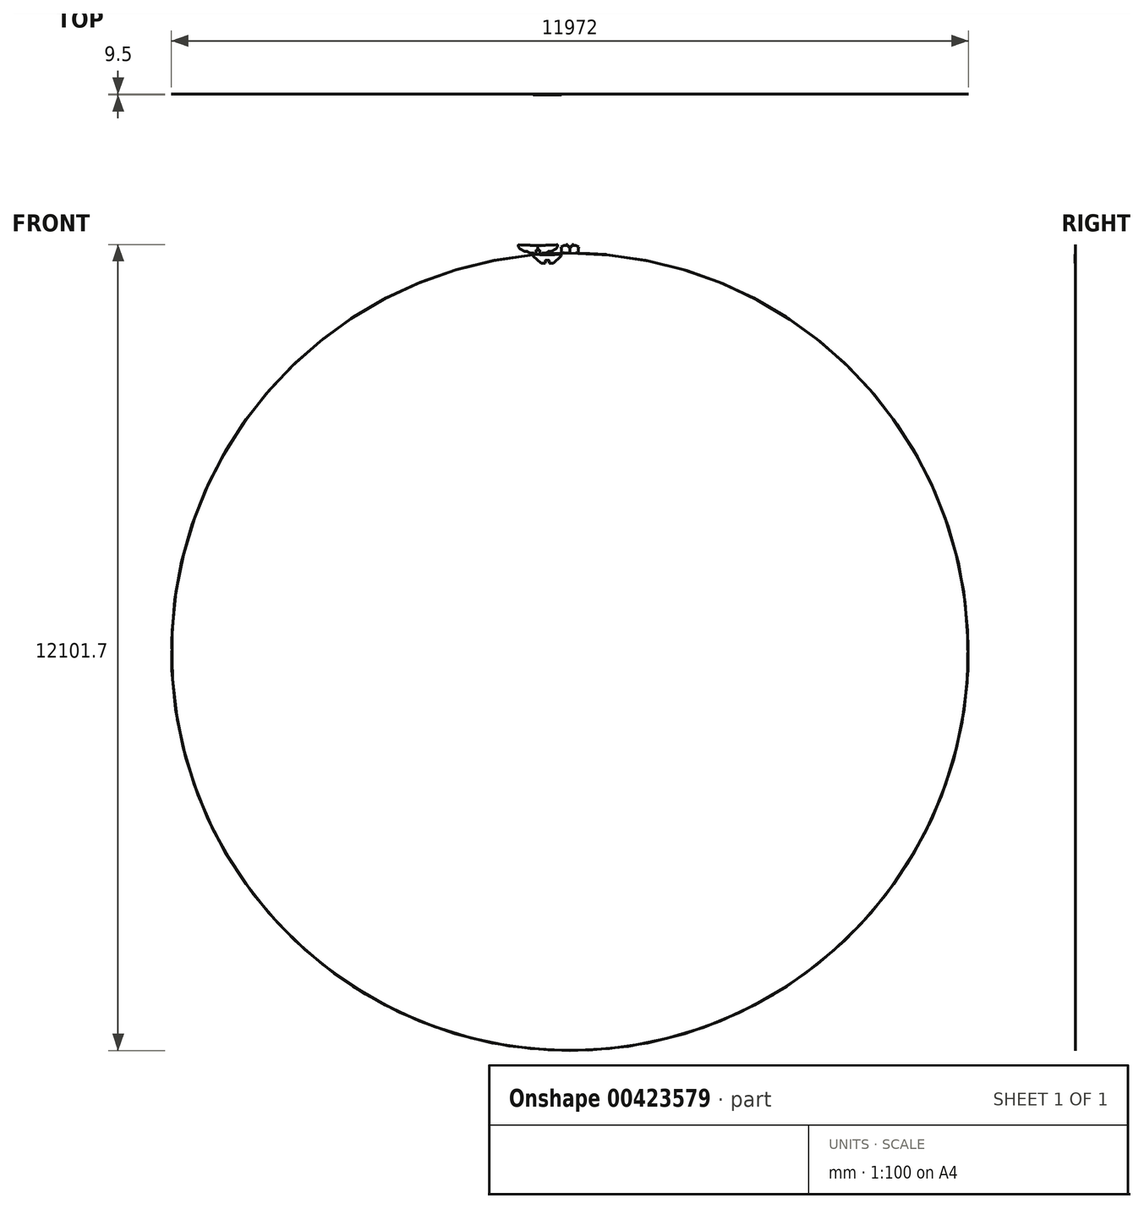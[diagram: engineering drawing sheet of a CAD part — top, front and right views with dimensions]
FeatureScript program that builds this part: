
annotation { "Feature Type Name" : "Feature", "Feature Type Description" : "" }
export const myFeature = defineFeature(function(context is Context, id is Id, definition is map)
    precondition{}
    {
        {
            assignVariable(context, id + "F0", {"name" : "eTole", "anyValue" : 1});
        }
        {
            assignVariable(context, id + "F1", {"name" : "eProfil", "anyValue" : 7});
        }
        {
            var Q0;
            Q0=qCreatedBy(makeId("Front.planeOp"),FACE);
            var sketch = newSketch(context, id + "F2", { "sketchPlane" : qUnion([Q0])});
            skLineSegment(sketch, "E0.bottom", {"start": v(-500, 75) * mm, "end": v(500, 75) * mm});
            skLineSegment(sketch, "E0.top", {"start": v(-500, -75) * mm, "end": v(500, -75) * mm});
            skLineSegment(sketch, "E0.left", {"start": v(-500, 75) * mm, "end": v(-500, -75) * mm});
            skLineSegment(sketch, "E0.right", {"start": v(500, 75) * mm, "end": v(500, -75) * mm});
            skCircle(sketch, "E1", {"center": v(-140, -3) * mm, "radius": 4 * mm});
            skCircle(sketch, "E2", {"center": v(340, 26) * mm, "radius": 4 * mm});
            skLineSegment(sketch, "E3.bottom", {"start": v(-255, -75) * mm, "end": v(261.67, -75) * mm});
            skLineSegment(sketch, "E3.top", {"start": v(-255, -225) * mm, "end": v(228.33, -225) * mm});
            skLineSegment(sketch, "E3.left", {"start": v(-255, -75) * mm, "end": v(-255, -225) * mm});
            skLineSegment(sketch, "E3.right", {"start": v(261.67, -75) * mm, "end": v(228.33, -225) * mm});
            skCircle(sketch, "E4", {"center": v(0, -155) * mm, "radius": 4 * mm});
            skLineSegment(sketch, "E5", {"start": v(-255, -150) * mm, "end": v(245, -150) * mm, "construction": true});
            skPoint(sketch, "E6", {"position": v(0, -105) * mm});
            skLineSegment(sketch, "E7", {"start": v(-255, -105) * mm, "end": v(255, -105) * mm, "construction": true});
            skSolve(sketch);
        }
        {
            var Q0;
            Q0=sQuery(id+"F2.wireOp",VERTEX,"E1.center");
            var Q1;
            Q1=qCreatedBy(makeId("Right.planeOp"),FACE);
            cPlane(context, id + "F3", {"entities" : qUnion([Q0, Q1]), "cplaneType" : CPlaneType.PLANE_POINT, "offset" : 25 * mm, "width" : 150 * mm, "height" : 150 * mm});
        }
        {
            var Q0;
            Q0=sQuery(id+"F2.wireOp",VERTEX,"E2.center");
            var Q1;
            Q1=qCreatedBy(makeId("Right.planeOp"),FACE);
            cPlane(context, id + "F4", {"entities" : qUnion([Q0, Q1]), "cplaneType" : CPlaneType.PLANE_POINT, "offset" : 25 * mm, "width" : 150 * mm, "height" : 150 * mm});
        }
        {
            var Q0;
            Q0=qCreatedBy(makeId("Front.planeOp"),FACE);
            var sketch = newSketch(context, id + "F5", { "sketchPlane" : qUnion([Q0])});
            skCircle(sketch, "E8.0", {"center": v(-140, -3) * mm, "radius": 4 * mm});
            skLineSegment(sketch, "E9.bottom", {"start": v(-164, -13) * mm, "end": v(-116, -13) * mm});
            skLineSegment(sketch, "E9.top", {"start": v(-164, -73) * mm, "end": v(-116, -73) * mm});
            skLineSegment(sketch, "E9.left", {"start": v(-170, -19) * mm, "end": v(-170, -67) * mm});
            skLineSegment(sketch, "E9.right", {"start": v(-110, -19) * mm, "end": v(-110, -67) * mm});
            skLineSegment(sketch, "E10", {"start": v(-140, -3) * mm, "end": v(-140, -73) * mm, "construction": true});
            skPoint(sketch, "E11.visualSharp", {"position": v(-170, -13) * mm});
            skArc(sketch, "E11.filletArc", {"start": v(-164, -13) * mm, "mid": v(-168.24, -14.76) * mm, "end": v(-170, -19) * mm});
            skPoint(sketch, "E12.visualSharp", {"position": v(-170, -73) * mm});
            skArc(sketch, "E12.filletArc", {"start": v(-170, -67) * mm, "mid": v(-168.24, -71.24) * mm, "end": v(-164, -73) * mm});
            skPoint(sketch, "E13.visualSharp", {"position": v(-110, -73) * mm});
            skArc(sketch, "E13.filletArc", {"start": v(-116, -73) * mm, "mid": v(-111.76, -71.24) * mm, "end": v(-110, -67) * mm});
            skPoint(sketch, "E14.visualSharp", {"position": v(-110, -13) * mm});
            skArc(sketch, "E14.filletArc", {"start": v(-110, -19) * mm, "mid": v(-111.76, -14.76) * mm, "end": v(-116, -13) * mm});
            skLineSegment(sketch, "E15.bottom", {"start": v(316, 96) * mm, "end": v(364, 96) * mm});
            skLineSegment(sketch, "E15.top", {"start": v(316, 36) * mm, "end": v(364, 36) * mm});
            skLineSegment(sketch, "E15.left", {"start": v(310, 90) * mm, "end": v(310, 42) * mm});
            skLineSegment(sketch, "E15.right", {"start": v(370, 90) * mm, "end": v(370, 42) * mm});
            skPoint(sketch, "E16.visualSharp", {"position": v(310, 96) * mm});
            skArc(sketch, "E16.filletArc", {"start": v(316, 96) * mm, "mid": v(311.76, 94.24) * mm, "end": v(310, 90) * mm});
            skPoint(sketch, "E17.visualSharp", {"position": v(310, 36) * mm});
            skArc(sketch, "E17.filletArc", {"start": v(310, 42) * mm, "mid": v(311.76, 37.76) * mm, "end": v(316, 36) * mm});
            skPoint(sketch, "E18.visualSharp", {"position": v(370, 36) * mm});
            skArc(sketch, "E18.filletArc", {"start": v(364, 36) * mm, "mid": v(368.24, 37.76) * mm, "end": v(370, 42) * mm});
            skPoint(sketch, "E19.visualSharp", {"position": v(370, 96) * mm});
            skArc(sketch, "E19.filletArc", {"start": v(370, 90) * mm, "mid": v(368.24, 94.24) * mm, "end": v(364, 96) * mm});
            skCircle(sketch, "E20.0", {"center": v(340, 26) * mm, "radius": 4 * mm});
            skLineSegment(sketch, "E21", {"start": v(340, 26) * mm, "end": v(340, 96) * mm, "construction": true});
            skLineSegment(sketch, "E22", {"start": v(-215, -73) * mm, "end": v(-215, 57) * mm, "construction": true});
            skLineSegment(sketch, "E23.MirrorCS", {"start": v(-65, -73) * mm, "end": v(-65, 57) * mm, "construction": true});
            skLineSegment(sketch, "E24.bottom", {"start": v(-80, -58) * mm, "end": v(-50, -58) * mm, "construction": true});
            skLineSegment(sketch, "E24.top", {"start": v(-80, -73) * mm, "end": v(-50, -73) * mm, "construction": true});
            skLineSegment(sketch, "E24.left", {"start": v(-80, -58) * mm, "end": v(-80, -73) * mm, "construction": true});
            skLineSegment(sketch, "E24.right", {"start": v(-50, -58) * mm, "end": v(-50, -73) * mm, "construction": true});
            skLineSegment(sketch, "E25.bottom", {"start": v(250, 96) * mm, "end": v(280, 96) * mm, "construction": true});
            skLineSegment(sketch, "E25.top", {"start": v(250, 81) * mm, "end": v(280, 81) * mm, "construction": true});
            skLineSegment(sketch, "E25.left", {"start": v(250, 96) * mm, "end": v(250, 81) * mm, "construction": true});
            skLineSegment(sketch, "E25.right", {"start": v(280, 96) * mm, "end": v(280, 81) * mm, "construction": true});
            skLineSegment(sketch, "E26", {"start": v(280, 81) * mm, "end": v(310, 81) * mm, "construction": true});
            skLineSegment(sketch, "E27", {"start": v(-110, -58) * mm, "end": v(-80, -58) * mm, "construction": true});
            skLineSegment(sketch, "E28", {"start": v(265, 96) * mm, "end": v(265, -34) * mm, "construction": true});
            skCircle(sketch, "E29.0", {"center": v(0, -155) * mm, "radius": 4 * mm});
            skLineSegment(sketch, "E30.bottom", {"start": v(-24, -165) * mm, "end": v(24, -165) * mm});
            skLineSegment(sketch, "E30.top", {"start": v(-24, -225) * mm, "end": v(24, -225) * mm});
            skLineSegment(sketch, "E30.left", {"start": v(-30, -171) * mm, "end": v(-30, -219) * mm});
            skLineSegment(sketch, "E30.right", {"start": v(30, -171) * mm, "end": v(30, -219) * mm});
            skLineSegment(sketch, "E31", {"start": v(0, -155) * mm, "end": v(0, -225) * mm, "construction": true});
            skPoint(sketch, "E32.visualSharp", {"position": v(-30, -225) * mm});
            skArc(sketch, "E32.filletArc", {"start": v(-30, -219) * mm, "mid": v(-28.24, -223.24) * mm, "end": v(-24, -225) * mm});
            skPoint(sketch, "E33.visualSharp", {"position": v(-30, -165) * mm});
            skArc(sketch, "E33.filletArc", {"start": v(-24, -165) * mm, "mid": v(-28.24, -166.76) * mm, "end": v(-30, -171) * mm});
            skPoint(sketch, "E34.visualSharp", {"position": v(30, -165) * mm});
            skArc(sketch, "E34.filletArc", {"start": v(30, -171) * mm, "mid": v(28.24, -166.76) * mm, "end": v(24, -165) * mm});
            skPoint(sketch, "E35.visualSharp", {"position": v(30, -225) * mm});
            skArc(sketch, "E35.filletArc", {"start": v(24, -225) * mm, "mid": v(28.24, -223.24) * mm, "end": v(30, -219) * mm});
            skLineSegment(sketch, "E36.MirrorCS", {"start": v(75, -225) * mm, "end": v(75, -95) * mm, "construction": true});
            skLineSegment(sketch, "E37.bottom", {"start": v(60, -210) * mm, "end": v(90, -210) * mm, "construction": true});
            skLineSegment(sketch, "E37.top", {"start": v(60, -225) * mm, "end": v(90, -225) * mm, "construction": true});
            skLineSegment(sketch, "E37.left", {"start": v(60, -210) * mm, "end": v(60, -225) * mm, "construction": true});
            skLineSegment(sketch, "E37.right", {"start": v(90, -210) * mm, "end": v(90, -225) * mm, "construction": true});
            skLineSegment(sketch, "E38", {"start": v(30, -210) * mm, "end": v(60, -210) * mm, "construction": true});
            skSolve(sketch);
        }
        {
            var Q0;
            Q0=qCreatedBy(makeId("Front.planeOp"),FACE);
            var sketch = newSketch(context, id + "F6", { "sketchPlane" : qUnion([Q0])});
            skLineSegment(sketch, "E39.0", {"start": v(-140, 1) * mm, "end": v(-140, 1) * mm});
            skLineSegment(sketch, "E39.1", {"start": v(-140, -13) * mm, "end": v(-116, -13) * mm});
            skLineSegment(sketch, "E39.2", {"start": v(-110, -19) * mm, "end": v(-110, -72.6) * mm});
            skArc(sketch, "E39.3", {"start": v(-110, -19) * mm, "mid": v(-111.76, -14.76) * mm, "end": v(-116, -13) * mm});
            skLineSegment(sketch, "E40", {"start": v(-140, -13) * mm, "end": v(-140, -7) * mm});
            skLineSegment(sketch, "E41.trimOffspring", {"start": v(-140, 1) * mm, "end": v(-140, 57) * mm});
            skLineSegment(sketch, "E42.0", {"start": v(-80, -58) * mm, "end": v(-80, -73) * mm, "construction": true});
            skLineSegment(sketch, "E42.1", {"start": v(-80, -73) * mm, "end": v(-50, -73) * mm, "construction": true});
            skLineSegment(sketch, "E43", {"start": v(-67.3, 57.64) * mm, "end": v(-65, -72.34) * mm, "construction": true});
            skLineSegment(sketch, "E44", {"start": v(-82.3, 57.38) * mm, "end": v(-52.3, 57.9) * mm, "construction": true});
            skLineSegment(sketch, "E45", {"start": v(-80, -72.6) * mm, "end": v(-50, -72.07) * mm, "construction": true});
            skLineSegment(sketch, "E46.0", {"start": v(-65, -73) * mm, "end": v(-65, 57) * mm, "construction": true});
            skArc(sketch, "E47", {"start": v(-140, 57) * mm, "mid": v(-112.14, 57.1) * mm, "end": v(-84.29, 57.38) * mm});
            skLineSegment(sketch, "E48", {"start": v(152.25, 67.4) * mm, "end": v(152.28, 67.07) * mm, "construction": true});
            skLineSegment(sketch, "E49", {"start": v(152.28, 67.07) * mm, "end": v(124.54, 65.2) * mm});
            skLineSegment(sketch, "E50", {"start": v(123.17, 64.51) * mm, "end": v(117.13, 57.6) * mm});
            skLineSegment(sketch, "E51", {"start": v(152.28, 67.07) * mm, "end": v(154.16, 39.33) * mm, "construction": true});
            skLineSegment(sketch, "E52", {"start": v(155.6, 40.12) * mm, "end": v(154.16, 39.33) * mm});
            skLineSegment(sketch, "E53", {"start": v(137.97, 66.4) * mm, "end": v(138, 66.1) * mm, "construction": true});
            skArc(sketch, "E54", {"start": v(117.13, 57.6) * mm, "mid": v(114.67, 60.86) * mm, "end": v(113.72, 64.83) * mm});
            skLineSegment(sketch, "E55", {"start": v(-80, -72.6) * mm, "end": v(-110, -72.6) * mm});
            skLineSegment(sketch, "E56", {"start": v(-80, -72.6) * mm, "end": v(-80.26, -57.6) * mm});
            skLineSegment(sketch, "E57", {"start": v(-80.26, -57.6) * mm, "end": v(-21.59, -56.57) * mm});
            skLineSegment(sketch, "E58", {"start": v(16.3, -35.9) * mm, "end": v(59.45, -35.13) * mm});
            skLineSegment(sketch, "E59", {"start": v(59.45, -35.13) * mm, "end": v(128.97, 2.8) * mm});
            skLineSegment(sketch, "E60", {"start": v(128.97, 2.8) * mm, "end": v(152.96, 38.68) * mm});
            skLineSegment(sketch, "E61", {"start": v(12.7, -35.58) * mm, "end": v(15.34, -34.14) * mm});
            skLineSegment(sketch, "E62", {"start": v(15.34, -34.14) * mm, "end": v(16.3, -35.9) * mm});
            skLineSegment(sketch, "E63", {"start": v(152.96, 38.68) * mm, "end": v(152, 40.44) * mm});
            skLineSegment(sketch, "E64", {"start": v(152, 40.44) * mm, "end": v(154.63, 41.87) * mm});
            skLineSegment(sketch, "E65", {"start": v(154.63, 41.87) * mm, "end": v(155.6, 40.12) * mm});
            skLineSegment(sketch, "E66.trimOffspring", {"start": v(152.96, 38.68) * mm, "end": v(16.3, -35.9) * mm, "construction": true});
            skLineSegment(sketch, "E67", {"start": v(-82.26, 55.41) * mm, "end": v(-81.96, 38.38) * mm});
            skLineSegment(sketch, "E68", {"start": v(-81.96, 38.38) * mm, "end": v(-80.96, 38.4) * mm});
            skLineSegment(sketch, "E69", {"start": v(-80.96, 38.4) * mm, "end": v(-81.23, 53.4) * mm});
            skLineSegment(sketch, "E70", {"start": v(-79.26, 55.43) * mm, "end": v(-55.26, 55.86) * mm});
            skLineSegment(sketch, "E71", {"start": v(-53.23, 53.9) * mm, "end": v(-52.96, 38.9) * mm});
            skLineSegment(sketch, "E72", {"start": v(-52.96, 38.9) * mm, "end": v(-51.96, 38.91) * mm});
            skLineSegment(sketch, "E73", {"start": v(-51.96, 38.91) * mm, "end": v(-52.27, 55.94) * mm});
            skLineSegment(sketch, "E74", {"start": v(154.41, 65.14) * mm, "end": v(155.2, 41.16) * mm});
            skArc(sketch, "E75", {"start": v(154.16, 39.33) * mm, "mid": v(154.93, 40.1) * mm, "end": v(155.2, 41.16) * mm});
            skArc(sketch, "E76", {"start": v(152.28, 67.07) * mm, "mid": v(153.75, 66.56) * mm, "end": v(154.41, 65.14) * mm});
            skArc(sketch, "E77.filletArc", {"start": v(124.54, 65.2) * mm, "mid": v(123.79, 64.99) * mm, "end": v(123.17, 64.51) * mm});
            skArc(sketch, "E78.trimOffspring", {"start": v(-50.3, 57.98) * mm, "mid": v(31.74, 60.59) * mm, "end": v(113.72, 64.83) * mm});
            skPoint(sketch, "E79.visualSharp", {"position": v(-81.26, 55.4) * mm});
            skArc(sketch, "E79.filletArc", {"start": v(-79.26, 55.43) * mm, "mid": v(-80.66, 54.82) * mm, "end": v(-81.23, 53.4) * mm});
            skPoint(sketch, "E80.visualSharp", {"position": v(-53.26, 55.9) * mm});
            skArc(sketch, "E80.filletArc", {"start": v(-53.23, 53.9) * mm, "mid": v(-53.84, 55.3) * mm, "end": v(-55.26, 55.86) * mm});
            skPoint(sketch, "E81.visualSharp", {"position": v(-82.3, 57.4) * mm});
            skArc(sketch, "E81.filletArc", {"start": v(-82.26, 55.41) * mm, "mid": v(-82.87, 56.81) * mm, "end": v(-84.29, 57.38) * mm});
            skPoint(sketch, "E82.visualSharp", {"position": v(-52.3, 57.94) * mm});
            skArc(sketch, "E82.filletArc", {"start": v(-50.3, 57.98) * mm, "mid": v(-51.7, 57.36) * mm, "end": v(-52.27, 55.94) * mm});
            skArc(sketch, "E83.0", {"start": v(-140, -7) * mm, "mid": v(-136, -3) * mm, "end": v(-140, 1) * mm});
            skLineSegment(sketch, "E84", {"start": v(12.7, -35.58) * mm, "end": v(13.66, -37.33) * mm});
            skLineSegment(sketch, "E85", {"start": v(13.66, -37.33) * mm, "end": v(-21.59, -56.57) * mm});
            skSolve(sketch);
        }
        {
            var Q0;
            Q0=qCreatedBy(makeId("Front.planeOp"),FACE);
            var sketch = newSketch(context, id + "F7", { "sketchPlane" : qUnion([Q0])});
            skLineSegment(sketch, "E86.0", {"start": v(0, -151) * mm, "end": v(0, -151) * mm});
            skLineSegment(sketch, "E87.0", {"start": v(0, -165) * mm, "end": v(24, -165) * mm});
            skArc(sketch, "E87.1", {"start": v(30, -171) * mm, "mid": v(28.24, -166.76) * mm, "end": v(24, -165) * mm});
            skLineSegment(sketch, "E87.2", {"start": v(30, -171) * mm, "end": v(30, -212.17) * mm});
            skLineSegment(sketch, "E88", {"start": v(0, -165) * mm, "end": v(0, -151) * mm});
            skLineSegment(sketch, "E89.trimOffspring", {"start": v(0, -151) * mm, "end": v(0, -82.5) * mm});
            skLineSegment(sketch, "E90.0", {"start": v(75, -225) * mm, "end": v(75, -95) * mm, "construction": true});
            skLineSegment(sketch, "E90.1", {"start": v(60, -225) * mm, "end": v(90, -225) * mm, "construction": true});
            skLineSegment(sketch, "E90.2", {"start": v(90, -210) * mm, "end": v(90, -225) * mm, "construction": true});
            skArc(sketch, "E91", {"start": v(0, -82.5) * mm, "mid": v(28.05, -82.42) * mm, "end": v(56.1, -82.18) * mm});
            skLineSegment(sketch, "E92", {"start": v(207.44, -78.17) * mm, "end": v(207.45, -78.5) * mm, "construction": true});
            skLineSegment(sketch, "E93", {"start": v(73.09, -81.96) * mm, "end": v(75, -211.95) * mm, "construction": true});
            skLineSegment(sketch, "E94", {"start": v(60, -212.17) * mm, "end": v(90, -211.73) * mm, "construction": true});
            skLineSegment(sketch, "E95", {"start": v(60, -212.17) * mm, "end": v(30, -212.17) * mm});
            skLineSegment(sketch, "E96", {"start": v(60, -212.17) * mm, "end": v(59.78, -197.17) * mm});
            skLineSegment(sketch, "E97", {"start": v(59.78, -197.17) * mm, "end": v(104.21, -196.52) * mm});
            skLineSegment(sketch, "E98", {"start": v(171.22, -86.97) * mm, "end": v(177.45, -80.24) * mm});
            skLineSegment(sketch, "E99", {"start": v(178.84, -79.6) * mm, "end": v(207.45, -78.5) * mm});
            skLineSegment(sketch, "E100", {"start": v(192.73, -79.06) * mm, "end": v(192.72, -78.76) * mm, "construction": true});
            skLineSegment(sketch, "E101", {"start": v(90, -211.73) * mm, "end": v(208.56, -107.1) * mm, "construction": true});
            skArc(sketch, "E102", {"start": v(171.22, -86.97) * mm, "mid": v(168.85, -83.65) * mm, "end": v(168, -79.66) * mm});
            skLineSegment(sketch, "E103", {"start": v(104.21, -196.52) * mm, "end": v(110.84, -190.67) * mm});
            skLineSegment(sketch, "E104", {"start": v(110.84, -190.67) * mm, "end": v(112.16, -192.17) * mm});
            skLineSegment(sketch, "E105", {"start": v(112.16, -192.17) * mm, "end": v(142.4, -192.17) * mm});
            skLineSegment(sketch, "E106", {"start": v(142.4, -192.17) * mm, "end": v(201.6, -139.93) * mm});
            skLineSegment(sketch, "E107", {"start": v(201.6, -139.93) * mm, "end": v(205.36, -109.94) * mm});
            skLineSegment(sketch, "E108", {"start": v(205.36, -109.94) * mm, "end": v(204.03, -108.44) * mm});
            skLineSegment(sketch, "E109", {"start": v(204.03, -108.44) * mm, "end": v(206.28, -106.45) * mm});
            skLineSegment(sketch, "E110", {"start": v(206.28, -106.45) * mm, "end": v(207.6, -107.95) * mm});
            skLineSegment(sketch, "E111", {"start": v(209.53, -80.4) * mm, "end": v(210.53, -104.39) * mm});
            skArc(sketch, "E112", {"start": v(209.53, -80.4) * mm, "mid": v(208.89, -79.02) * mm, "end": v(207.45, -78.5) * mm});
            skLineSegment(sketch, "E113", {"start": v(207.6, -107.95) * mm, "end": v(209.86, -105.97) * mm});
            skArc(sketch, "E114", {"start": v(210.53, -104.39) * mm, "mid": v(210.37, -105.25) * mm, "end": v(209.86, -105.97) * mm});
            skLineSegment(sketch, "E115.trimOffspring", {"start": v(207.45, -78.5) * mm, "end": v(208.56, -107.1) * mm, "construction": true});
            skLineSegment(sketch, "E116", {"start": v(58.1, -82.18) * mm, "end": v(88.09, -81.74) * mm, "construction": true});
            skLineSegment(sketch, "E117", {"start": v(58.12, -84.15) * mm, "end": v(58.34, -99.18) * mm});
            skLineSegment(sketch, "E118", {"start": v(58.34, -99.18) * mm, "end": v(59.34, -99.17) * mm});
            skLineSegment(sketch, "E119", {"start": v(59.15, -86.17) * mm, "end": v(59.34, -99.17) * mm});
            skLineSegment(sketch, "E120", {"start": v(61.12, -84.14) * mm, "end": v(85.12, -83.79) * mm});
            skLineSegment(sketch, "E121", {"start": v(87.34, -98.75) * mm, "end": v(87.15, -85.76) * mm});
            skLineSegment(sketch, "E122", {"start": v(87.34, -98.75) * mm, "end": v(88.34, -98.74) * mm});
            skLineSegment(sketch, "E123", {"start": v(88.34, -98.74) * mm, "end": v(88.12, -83.71) * mm});
            skArc(sketch, "E124.trimOffspring", {"start": v(90.08, -81.68) * mm, "mid": v(129.05, -80.82) * mm, "end": v(168, -79.66) * mm});
            skPoint(sketch, "E125.visualSharp", {"position": v(59.12, -84.17) * mm});
            skArc(sketch, "E125.filletArc", {"start": v(61.12, -84.14) * mm, "mid": v(59.71, -84.75) * mm, "end": v(59.15, -86.17) * mm});
            skPoint(sketch, "E126.visualSharp", {"position": v(87.12, -83.76) * mm});
            skArc(sketch, "E126.filletArc", {"start": v(87.15, -85.76) * mm, "mid": v(86.54, -84.35) * mm, "end": v(85.12, -83.79) * mm});
            skPoint(sketch, "E127.visualSharp", {"position": v(58.09, -82.16) * mm});
            skArc(sketch, "E127.filletArc", {"start": v(58.12, -84.15) * mm, "mid": v(57.52, -82.75) * mm, "end": v(56.1, -82.18) * mm});
            skPoint(sketch, "E128.visualSharp", {"position": v(88.09, -81.72) * mm});
            skArc(sketch, "E128.filletArc", {"start": v(90.08, -81.68) * mm, "mid": v(88.68, -82.3) * mm, "end": v(88.12, -83.71) * mm});
            skArc(sketch, "E129.filletArc", {"start": v(178.84, -79.6) * mm, "mid": v(178.08, -79.78) * mm, "end": v(177.45, -80.24) * mm});
            skSolve(sketch);
        }
        {
            var Q0;
            Q0=qCreatedBy(makeId("Front.planeOp"),FACE);
            var sketch = newSketch(context, id + "F8", { "sketchPlane" : qUnion([Q0])});
            skLineSegment(sketch, "E130.0", {"start": v(310, 69.52) * mm, "end": v(310, 42) * mm});
            skLineSegment(sketch, "E130.1", {"start": v(316, 36) * mm, "end": v(340, 36) * mm});
            skLineSegment(sketch, "E130.2", {"start": v(340, 30) * mm, "end": v(340, 30) * mm});
            skArc(sketch, "E130.3", {"start": v(310, 42) * mm, "mid": v(311.76, 37.76) * mm, "end": v(316, 36) * mm});
            skLineSegment(sketch, "E130.4", {"start": v(250, 96) * mm, "end": v(280, 96) * mm, "construction": true});
            skLineSegment(sketch, "E130.5", {"start": v(265, 96) * mm, "end": v(265, -34) * mm, "construction": true});
            skLineSegment(sketch, "E130.6", {"start": v(280, 96) * mm, "end": v(280, 81) * mm, "construction": true});
            skLineSegment(sketch, "E131", {"start": v(340, 36) * mm, "end": v(340, 30) * mm});
            skLineSegment(sketch, "E132.trimOffspring", {"start": v(340, 22) * mm, "end": v(340, -60.2) * mm});
            skArc(sketch, "E133", {"start": v(340, -60.2) * mm, "mid": v(311.8, -60.27) * mm, "end": v(283.59, -60.47) * mm});
            skLineSegment(sketch, "E134", {"start": v(266.6, -60.65) * mm, "end": v(265, 69.34) * mm, "construction": true});
            skLineSegment(sketch, "E135", {"start": v(250, 69.16) * mm, "end": v(280, 69.52) * mm, "construction": true});
            skLineSegment(sketch, "E136", {"start": v(280, 69.52) * mm, "end": v(310, 69.52) * mm});
            skLineSegment(sketch, "E137", {"start": v(215, -61.5) * mm, "end": v(215, -61.2) * mm, "construction": true});
            skLineSegment(sketch, "E138", {"start": v(246.76, -53.52) * mm, "end": v(240.4, -60.13) * mm});
            skLineSegment(sketch, "E139", {"start": v(239, -60.74) * mm, "end": v(215, -61.2) * mm});
            skLineSegment(sketch, "E140", {"start": v(215, -61.2) * mm, "end": v(214.42, -30.35) * mm, "construction": true});
            skLineSegment(sketch, "E141", {"start": v(240.89, 54.04) * mm, "end": v(280.18, 54.53) * mm});
            skLineSegment(sketch, "E142", {"start": v(280.18, 54.53) * mm, "end": v(280, 69.52) * mm});
            skLineSegment(sketch, "E143", {"start": v(227.41, -60.96) * mm, "end": v(227.42, -61.26) * mm, "construction": true});
            skArc(sketch, "E144", {"start": v(246.76, -53.52) * mm, "mid": v(249.06, -56.88) * mm, "end": v(249.83, -60.88) * mm});
            skLineSegment(sketch, "E145", {"start": v(251.6, -60.83) * mm, "end": v(281.6, -60.47) * mm, "construction": true});
            skLineSegment(sketch, "E146", {"start": v(251.37, -42.71) * mm, "end": v(251.57, -58.86) * mm});
            skLineSegment(sketch, "E147", {"start": v(251.37, -42.71) * mm, "end": v(252.37, -42.7) * mm});
            skLineSegment(sketch, "E148", {"start": v(252.37, -42.7) * mm, "end": v(252.55, -56.82) * mm});
            skLineSegment(sketch, "E149", {"start": v(254.57, -58.8) * mm, "end": v(278.57, -58.5) * mm});
            skLineSegment(sketch, "E150", {"start": v(280.54, -56.48) * mm, "end": v(280.37, -42.36) * mm});
            skLineSegment(sketch, "E151", {"start": v(280.37, -42.36) * mm, "end": v(281.37, -42.35) * mm});
            skLineSegment(sketch, "E152", {"start": v(281.57, -58.5) * mm, "end": v(281.37, -42.35) * mm});
            skArc(sketch, "E153.trimOffspring", {"start": v(249.6, -60.88) * mm, "mid": v(430.29, -12031.52) * mm, "end": v(249.83, -60.88) * mm});
            skLineSegment(sketch, "E154", {"start": v(243.24, 54.07) * mm, "end": v(242.33, 51.21) * mm});
            skLineSegment(sketch, "E155", {"start": v(242.33, 51.21) * mm, "end": v(240.43, 51.82) * mm});
            skLineSegment(sketch, "E156", {"start": v(240.43, 51.82) * mm, "end": v(207.85, 35.55) * mm});
            skLineSegment(sketch, "E157", {"start": v(207.85, 35.55) * mm, "end": v(213.74, 6.06) * mm});
            skLineSegment(sketch, "E158", {"start": v(213.74, 6.06) * mm, "end": v(214.42, -30.35) * mm});
            skLineSegment(sketch, "E159", {"start": v(214.42, -30.35) * mm, "end": v(216.1, -31.43) * mm});
            skLineSegment(sketch, "E160", {"start": v(216.1, -31.43) * mm, "end": v(214.5, -33.95) * mm});
            skLineSegment(sketch, "E161", {"start": v(214.5, -33.95) * mm, "end": v(213.09, -33.45) * mm});
            skLineSegment(sketch, "E162", {"start": v(213.09, -33.45) * mm, "end": v(212.68, -34.4) * mm});
            skLineSegment(sketch, "E163", {"start": v(212.97, -59.23) * mm, "end": v(212.51, -35.23) * mm});
            skArc(sketch, "E164", {"start": v(215, -61.2) * mm, "mid": v(213.58, -60.63) * mm, "end": v(212.97, -59.23) * mm});
            skPoint(sketch, "E165.visualSharp", {"position": v(212.5, -34.8) * mm});
            skArc(sketch, "E165.filletArc", {"start": v(212.68, -34.4) * mm, "mid": v(212.55, -34.81) * mm, "end": v(212.51, -35.23) * mm});
            skArc(sketch, "E166.0", {"start": v(340, 30) * mm, "mid": v(336, 26) * mm, "end": v(340, 22) * mm});
            skPoint(sketch, "E167.visualSharp", {"position": v(251.6, -60.85) * mm});
            skArc(sketch, "E167.filletArc", {"start": v(249.6, -60.88) * mm, "mid": v(251, -60.28) * mm, "end": v(251.57, -58.86) * mm});
            skPoint(sketch, "E168.visualSharp", {"position": v(252.57, -58.82) * mm});
            skArc(sketch, "E168.filletArc", {"start": v(252.55, -56.82) * mm, "mid": v(253.15, -58.23) * mm, "end": v(254.57, -58.8) * mm});
            skPoint(sketch, "E169.visualSharp", {"position": v(280.57, -58.48) * mm});
            skArc(sketch, "E169.filletArc", {"start": v(278.57, -58.5) * mm, "mid": v(279.98, -57.9) * mm, "end": v(280.54, -56.48) * mm});
            skPoint(sketch, "E170.visualSharp", {"position": v(281.6, -60.48) * mm});
            skArc(sketch, "E170.filletArc", {"start": v(281.57, -58.5) * mm, "mid": v(282.17, -59.9) * mm, "end": v(283.59, -60.47) * mm});
            skArc(sketch, "E171.filletArc", {"start": v(239, -60.74) * mm, "mid": v(239.76, -60.57) * mm, "end": v(240.4, -60.13) * mm});
            skLineSegment(sketch, "E172", {"start": v(250, 69.16) * mm, "end": v(214.42, -30.35) * mm, "construction": true});
            skLineSegment(sketch, "E173", {"start": v(214.96, -59.2) * mm, "end": v(238.96, -58.74) * mm, "construction": true});
            skSolve(sketch);
        }
        {
            var Q0;
            Q0=qCreatedBy(makeId("Front.planeOp"),FACE);
            var sketch = newSketch(context, id + "F9", { "sketchPlane" : qUnion([Q0])});
            skLineSegment(sketch, "E174.0", {"start": v(-140, 1) * mm, "end": v(-140, 57) * mm, "construction": true});
            skLineSegment(sketch, "E175.0", {"start": v(-80, -72.6) * mm, "end": v(-80.26, -57.6) * mm});
            skLineSegment(sketch, "E175.1", {"start": v(-80.26, -57.6) * mm, "end": v(-21.59, -56.57) * mm});
            skLineSegment(sketch, "E175.2", {"start": v(59.45, -35.13) * mm, "end": v(128.97, 2.8) * mm});
            skLineSegment(sketch, "E175.3", {"start": v(128.97, 2.8) * mm, "end": v(152.96, 38.68) * mm});
            skLineSegment(sketch, "E175.4", {"start": v(155.24, 39.92) * mm, "end": v(152.96, 38.68) * mm});
            skLineSegment(sketch, "E176.MirrorCS", {"start": v(-435.24, 39.92) * mm, "end": v(-432.96, 38.68) * mm});
            skLineSegment(sketch, "E177.MirrorCS", {"start": v(-200, -72.6) * mm, "end": v(-199.74, -57.6) * mm});
            skLineSegment(sketch, "E178.MirrorCS", {"start": v(-339.45, -35.13) * mm, "end": v(-408.97, 2.8) * mm});
            skLineSegment(sketch, "E179.MirrorCS", {"start": v(-199.74, -57.6) * mm, "end": v(-258.41, -56.57) * mm});
            skLineSegment(sketch, "E180.MirrorCS", {"start": v(-408.97, 2.8) * mm, "end": v(-432.96, 38.68) * mm});
            skLineSegment(sketch, "E181", {"start": v(-200, -72.6) * mm, "end": v(-170, -72.6) * mm});
            skLineSegment(sketch, "E182.0", {"start": v(-500, 75) * mm, "end": v(-500, -75) * mm});
            skLineSegment(sketch, "E182.1", {"start": v(-500, -75) * mm, "end": v(500, -75) * mm});
            skLineSegment(sketch, "E182.2", {"start": v(-500, 75) * mm, "end": v(500, 75) * mm});
            skLineSegment(sketch, "E182.3", {"start": v(500, 75) * mm, "end": v(500, -75) * mm});
            skLineSegment(sketch, "E183.0", {"start": v(340, 22) * mm, "end": v(340, -60.2) * mm, "construction": true});
            skLineSegment(sketch, "E184.0", {"start": v(280, 69.52) * mm, "end": v(310, 69.52) * mm});
            skLineSegment(sketch, "E184.1", {"start": v(280.18, 54.53) * mm, "end": v(280, 69.52) * mm});
            skLineSegment(sketch, "E184.2", {"start": v(244.98, 54.1) * mm, "end": v(280.18, 54.53) * mm});
            skLineSegment(sketch, "E184.3", {"start": v(244.98, 54.1) * mm, "end": v(207.85, 35.55) * mm});
            skLineSegment(sketch, "E184.4", {"start": v(207.85, 35.55) * mm, "end": v(213.74, 6.06) * mm});
            skLineSegment(sketch, "E184.5", {"start": v(213.74, 6.06) * mm, "end": v(214.42, -30.35) * mm});
            skLineSegment(sketch, "E184.6", {"start": v(213, -61.23) * mm, "end": v(212.51, -35.23) * mm});
            skLineSegment(sketch, "E184.7", {"start": v(340, -58.84) * mm, "end": v(213, -61.23) * mm});
            skLineSegment(sketch, "E185.0", {"start": v(154.34, 67.21) * mm, "end": v(155.24, 39.92) * mm});
            skLineSegment(sketch, "E185.1", {"start": v(154.34, 67.21) * mm, "end": v(-140, 47.27) * mm});
            skLineSegment(sketch, "E186", {"start": v(212.51, -35.23) * mm, "end": v(214.42, -30.35) * mm});
            skLineSegment(sketch, "E187.MirrorCS", {"start": v(340, -58.84) * mm, "end": v(467, -61.23) * mm});
            skLineSegment(sketch, "E188.MirrorCS", {"start": v(467, -61.23) * mm, "end": v(467.49, -35.23) * mm});
            skLineSegment(sketch, "E189.MirrorCS", {"start": v(466.26, 6.06) * mm, "end": v(465.58, -30.35) * mm});
            skLineSegment(sketch, "E190.MirrorCS", {"start": v(467.49, -35.23) * mm, "end": v(465.58, -30.35) * mm});
            skLineSegment(sketch, "E191.MirrorCS", {"start": v(472.15, 35.55) * mm, "end": v(466.26, 6.06) * mm});
            skLineSegment(sketch, "E192.MirrorCS", {"start": v(435.02, 54.1) * mm, "end": v(472.15, 35.55) * mm});
            skLineSegment(sketch, "E193.MirrorCS", {"start": v(435.02, 54.1) * mm, "end": v(399.82, 54.53) * mm});
            skLineSegment(sketch, "E194.MirrorCS", {"start": v(400, 69.52) * mm, "end": v(370, 69.52) * mm});
            skLineSegment(sketch, "E195.MirrorCS", {"start": v(399.82, 54.53) * mm, "end": v(400, 69.52) * mm});
            skLineSegment(sketch, "E196.MirrorCS", {"start": v(-434.34, 67.21) * mm, "end": v(-140, 47.27) * mm});
            skLineSegment(sketch, "E197.MirrorCS", {"start": v(-434.34, 67.21) * mm, "end": v(-435.24, 39.92) * mm});
            skLineSegment(sketch, "E198.0", {"start": v(16.3, -35.9) * mm, "end": v(-21.59, -56.57) * mm});
            skLineSegment(sketch, "E198.1", {"start": v(16.3, -35.9) * mm, "end": v(59.45, -35.13) * mm});
            skLineSegment(sketch, "E199.MirrorCS", {"start": v(-296.3, -35.9) * mm, "end": v(-258.41, -56.57) * mm});
            skLineSegment(sketch, "E200.MirrorCS", {"start": v(-296.3, -35.9) * mm, "end": v(-339.45, -35.13) * mm});
            skLineSegment(sketch, "E201.0", {"start": v(0, -165) * mm, "end": v(24, -165) * mm});
            skLineSegment(sketch, "E201.1", {"start": v(30, -171) * mm, "end": v(30, -212.17) * mm});
            skArc(sketch, "E201.2", {"start": v(30, -171) * mm, "mid": v(28.24, -166.76) * mm, "end": v(24, -165) * mm});
            skLineSegment(sketch, "E201.3", {"start": v(60, -212.17) * mm, "end": v(30, -212.17) * mm});
            skLineSegment(sketch, "E201.4", {"start": v(59.78, -197.17) * mm, "end": v(104.21, -196.52) * mm});
            skLineSegment(sketch, "E201.5", {"start": v(60, -212.17) * mm, "end": v(59.78, -197.17) * mm});
            skLineSegment(sketch, "E201.6", {"start": v(104.21, -196.52) * mm, "end": v(109.14, -192.17) * mm});
            skLineSegment(sketch, "E201.7", {"start": v(109.14, -192.17) * mm, "end": v(142.4, -192.17) * mm});
            skLineSegment(sketch, "E201.8", {"start": v(142.4, -192.17) * mm, "end": v(201.6, -139.93) * mm});
            skLineSegment(sketch, "E201.9", {"start": v(201.6, -139.93) * mm, "end": v(205.36, -109.94) * mm});
            skLineSegment(sketch, "E201.10", {"start": v(205.36, -109.94) * mm, "end": v(210.57, -105.34) * mm});
            skLineSegment(sketch, "E201.11", {"start": v(209.45, -78.41) * mm, "end": v(210.57, -105.34) * mm});
            skLineSegment(sketch, "E201.12", {"start": v(0, -86.54) * mm, "end": v(209.45, -78.41) * mm});
            skLineSegment(sketch, "E202.MirrorCS", {"start": v(0, -86.54) * mm, "end": v(-209.45, -78.41) * mm});
            skArc(sketch, "E203.MirrorCS", {"start": v(-30, -171) * mm, "mid": v(-28.24, -166.76) * mm, "end": v(-24, -165) * mm});
            skLineSegment(sketch, "E204.MirrorCS", {"start": v(-205.36, -109.94) * mm, "end": v(-210.57, -105.34) * mm});
            skLineSegment(sketch, "E205.MirrorCS", {"start": v(-104.21, -196.52) * mm, "end": v(-109.14, -192.17) * mm});
            skLineSegment(sketch, "E206.MirrorCS", {"start": v(0, -165) * mm, "end": v(-24, -165) * mm});
            skLineSegment(sketch, "E207.MirrorCS", {"start": v(-201.6, -139.93) * mm, "end": v(-205.36, -109.94) * mm});
            skLineSegment(sketch, "E208.MirrorCS", {"start": v(-142.4, -192.17) * mm, "end": v(-201.6, -139.93) * mm});
            skLineSegment(sketch, "E209.MirrorCS", {"start": v(-30, -171) * mm, "end": v(-30, -212.17) * mm});
            skLineSegment(sketch, "E210.MirrorCS", {"start": v(-60, -212.17) * mm, "end": v(-30, -212.17) * mm});
            skLineSegment(sketch, "E211.MirrorCS", {"start": v(-59.78, -197.17) * mm, "end": v(-104.21, -196.52) * mm});
            skLineSegment(sketch, "E212.MirrorCS", {"start": v(-60, -212.17) * mm, "end": v(-59.78, -197.17) * mm});
            skLineSegment(sketch, "E213.MirrorCS", {"start": v(-109.14, -192.17) * mm, "end": v(-142.4, -192.17) * mm});
            skLineSegment(sketch, "E214.MirrorCS", {"start": v(-209.45, -78.41) * mm, "end": v(-210.57, -105.34) * mm});
            skLineSegment(sketch, "E215.0", {"start": v(-255, -75) * mm, "end": v(-255, -225) * mm});
            skLineSegment(sketch, "E215.1", {"start": v(-255, -225) * mm, "end": v(228.33, -225) * mm});
            skLineSegment(sketch, "E215.2", {"start": v(261.67, -75) * mm, "end": v(228.33, -225) * mm});
            skLineSegment(sketch, "E216.0", {"start": v(-140, -13) * mm, "end": v(-116, -13) * mm});
            skArc(sketch, "E216.1", {"start": v(-110, -19) * mm, "mid": v(-111.76, -14.76) * mm, "end": v(-116, -13) * mm});
            skLineSegment(sketch, "E216.2", {"start": v(-110, -19) * mm, "end": v(-110, -72.6) * mm});
            skLineSegment(sketch, "E217.MirrorCS", {"start": v(-140, -13) * mm, "end": v(-164, -13) * mm});
            skLineSegment(sketch, "E218.MirrorCS", {"start": v(-170, -19) * mm, "end": v(-170, -72.6) * mm});
            skArc(sketch, "E219.MirrorCS", {"start": v(-170, -19) * mm, "mid": v(-168.24, -14.76) * mm, "end": v(-164, -13) * mm});
            skLineSegment(sketch, "E220.trimOffspring", {"start": v(-110, -72.6) * mm, "end": v(-80, -72.6) * mm});
            skLineSegment(sketch, "E221.0", {"start": v(310, 69.52) * mm, "end": v(310, 42) * mm});
            skLineSegment(sketch, "E221.1", {"start": v(316, 36) * mm, "end": v(340, 36) * mm});
            skArc(sketch, "E222.0", {"start": v(310, 42) * mm, "mid": v(311.76, 37.76) * mm, "end": v(316, 36) * mm});
            skLineSegment(sketch, "E223.MirrorCS", {"start": v(364, 36) * mm, "end": v(340, 36) * mm});
            skLineSegment(sketch, "E224.MirrorCS", {"start": v(370, 69.52) * mm, "end": v(370, 42) * mm});
            skArc(sketch, "E225.MirrorCS", {"start": v(370, 42) * mm, "mid": v(368.24, 37.76) * mm, "end": v(364, 36) * mm});
            skSolve(sketch);
        }
        {
            var Q0;
            Q0=qCreatedBy(makeId("Front.planeOp"),FACE);
            var sketch = newSketch(context, id + "F10", { "sketchPlane" : qUnion([Q0])});
            skLineSegment(sketch, "E226.0", {"start": v(-462, -75) * mm, "end": v(-338, -75) * mm});
            skLineSegment(sketch, "E226.1", {"start": v(-500, 32.5) * mm, "end": v(-500, -46.5) * mm});
            skLineSegment(sketch, "E227.0", {"start": v(-408.97, 2.8) * mm, "end": v(-428.83, 32.5) * mm});
            skLineSegment(sketch, "E227.1", {"start": v(-339.45, -35.13) * mm, "end": v(-408.97, 2.8) * mm});
            skLineSegment(sketch, "E227.2", {"start": v(-296.3, -35.9) * mm, "end": v(-339.45, -35.13) * mm});
            skLineSegment(sketch, "E227.3", {"start": v(-300, -33.87) * mm, "end": v(-296.3, -35.9) * mm});
            skLineSegment(sketch, "E228", {"start": v(-500, -46.5) * mm, "end": v(-462, -46.5) * mm});
            skLineSegment(sketch, "E229", {"start": v(-462, -46.5) * mm, "end": v(-462, -75) * mm});
            skLineSegment(sketch, "E230", {"start": v(-300, -46.5) * mm, "end": v(-300, -33.87) * mm});
            skLineSegment(sketch, "E231", {"start": v(-300, -46.5) * mm, "end": v(-338, -46.5) * mm});
            skLineSegment(sketch, "E232", {"start": v(-338, -46.5) * mm, "end": v(-338, -75) * mm});
            skLineSegment(sketch, "E233", {"start": v(-428.83, 32.5) * mm, "end": v(-500, 32.5) * mm});
            skLineSegment(sketch, "E234", {"start": v(-481.28, -46.5) * mm, "end": v(-481.28, -24) * mm, "construction": true});
            skLineSegment(sketch, "E235", {"start": v(-481.28, -24) * mm, "end": v(-481.28, 21) * mm, "construction": true});
            skCircle(sketch, "E236", {"center": v(-481.28, -24) * mm, "radius": 3 * mm});
            skCircle(sketch, "E237", {"center": v(-481.28, 21) * mm, "radius": 3 * mm});
            skLineSegment(sketch, "E238", {"start": v(-481.28, -24) * mm, "end": v(-462, -24) * mm, "construction": true});
            skLineSegment(sketch, "E239", {"start": v(-462, -46.5) * mm, "end": v(-338, -46.5) * mm, "construction": true});
            skPoint(sketch, "E240.orphan", {"position": v(-500, -75) * mm});
            skLineSegment(sketch, "E241", {"start": v(-462, -65.78) * mm, "end": v(-338, -65.78) * mm, "construction": true});
            skArc(sketch, "E242", {"start": v(-453, -62.78) * mm, "mid": v(-456, -65.78) * mm, "end": v(-453, -68.78) * mm});
            skArc(sketch, "E243", {"start": v(-447, -62.78) * mm, "mid": v(-444, -65.78) * mm, "end": v(-447, -68.78) * mm});
            skLineSegment(sketch, "E244", {"start": v(-453, -62.78) * mm, "end": v(-447, -62.78) * mm});
            skLineSegment(sketch, "E245", {"start": v(-453, -68.78) * mm, "end": v(-447, -68.78) * mm});
            skArc(sketch, "E246.1.0.0", {"start": v(-403, -62.78) * mm, "mid": v(-406, -65.78) * mm, "end": v(-403, -68.78) * mm});
            skLineSegment(sketch, "E246.1.0.1", {"start": v(-403, -62.78) * mm, "end": v(-397, -62.78) * mm});
            skArc(sketch, "E246.1.0.2", {"start": v(-397, -62.78) * mm, "mid": v(-394, -65.78) * mm, "end": v(-397, -68.78) * mm});
            skLineSegment(sketch, "E246.1.0.3", {"start": v(-403, -68.78) * mm, "end": v(-397, -68.78) * mm});
            skArc(sketch, "E246.2.0.0", {"start": v(-353, -62.78) * mm, "mid": v(-356, -65.78) * mm, "end": v(-353, -68.78) * mm});
            skLineSegment(sketch, "E246.2.0.1", {"start": v(-353, -62.78) * mm, "end": v(-347, -62.78) * mm});
            skArc(sketch, "E246.2.0.2", {"start": v(-347, -62.78) * mm, "mid": v(-344, -65.78) * mm, "end": v(-347, -68.78) * mm});
            skLineSegment(sketch, "E246.2.0.3", {"start": v(-353, -68.78) * mm, "end": v(-347, -68.78) * mm});
            skLineSegment(sketch, "E246.direction1", {"start": v(-453, -68.78) * mm, "end": v(-403, -68.78) * mm, "construction": true});
            skLineSegment(sketch, "E247", {"start": v(-453, -65.78) * mm, "end": v(-453, -46.5) * mm, "construction": true});
            skLineSegment(sketch, "E248", {"start": v(-462, -46.5) * mm, "end": v(-462, 82.1) * mm, "construction": true});
            skLineSegment(sketch, "E249.0", {"start": v(59.45, -35.13) * mm, "end": v(128.97, 2.8) * mm});
            skLineSegment(sketch, "E249.1", {"start": v(16.3, -35.9) * mm, "end": v(59.45, -35.13) * mm});
            skLineSegment(sketch, "E249.2", {"start": v(24.64, -31.34) * mm, "end": v(16.3, -35.9) * mm});
            skLineSegment(sketch, "E249.3", {"start": v(213.8, 2.8) * mm, "end": v(214.42, -30.35) * mm});
            skLineSegment(sketch, "E250.0", {"start": v(213, -61.23) * mm, "end": v(212.51, -35.23) * mm});
            skLineSegment(sketch, "E251", {"start": v(-142.79, -75) * mm, "end": v(-142.79, 0) * mm, "construction": true});
            skLineSegment(sketch, "E252.MirrorCS", {"start": v(52.42, -46.5) * mm, "end": v(52.42, -75) * mm});
            skArc(sketch, "E253.MirrorCS", {"start": v(61.42, -62.78) * mm, "mid": v(58.42, -65.78) * mm, "end": v(61.42, -68.78) * mm});
            skLineSegment(sketch, "E254.MirrorCS", {"start": v(67.42, -62.78) * mm, "end": v(61.42, -62.78) * mm});
            skArc(sketch, "E255.MirrorCS", {"start": v(67.42, -62.78) * mm, "mid": v(70.42, -65.78) * mm, "end": v(67.42, -68.78) * mm});
            skLineSegment(sketch, "E256.MirrorCS", {"start": v(67.42, -68.78) * mm, "end": v(61.42, -68.78) * mm});
            skArc(sketch, "E257.MirrorCS", {"start": v(111.42, -62.78) * mm, "mid": v(108.42, -65.78) * mm, "end": v(111.42, -68.78) * mm});
            skLineSegment(sketch, "E258.MirrorCS", {"start": v(117.42, -62.78) * mm, "end": v(111.42, -62.78) * mm});
            skArc(sketch, "E259.MirrorCS", {"start": v(117.42, -62.78) * mm, "mid": v(120.42, -65.78) * mm, "end": v(117.42, -68.78) * mm});
            skLineSegment(sketch, "E260.MirrorCS", {"start": v(117.42, -68.78) * mm, "end": v(111.42, -68.78) * mm});
            skLineSegment(sketch, "E261.MirrorCS", {"start": v(167.42, -62.78) * mm, "end": v(161.42, -62.78) * mm});
            skArc(sketch, "E262.MirrorCS", {"start": v(161.42, -62.78) * mm, "mid": v(158.42, -65.78) * mm, "end": v(161.42, -68.78) * mm});
            skArc(sketch, "E263.MirrorCS", {"start": v(167.42, -62.78) * mm, "mid": v(170.42, -65.78) * mm, "end": v(167.42, -68.78) * mm});
            skLineSegment(sketch, "E264.MirrorCS", {"start": v(176.42, -46.5) * mm, "end": v(176.42, -75) * mm});
            skLineSegment(sketch, "E265.MirrorCS", {"start": v(214.42, -46.5) * mm, "end": v(176.42, -46.5) * mm});
            skCircle(sketch, "E266.MirrorC", {"center": v(195.7, -24) * mm, "radius": 3 * mm});
            skLineSegment(sketch, "E267.MirrorCS", {"start": v(176.42, -46.5) * mm, "end": v(176.42, 28.7) * mm, "construction": true});
            skLineSegment(sketch, "E268.MirrorCS", {"start": v(176.42, -46.5) * mm, "end": v(52.42, -46.5) * mm, "construction": true});
            skLineSegment(sketch, "E269.MirrorCS", {"start": v(24.64, -46.5) * mm, "end": v(52.42, -46.5) * mm});
            skLineSegment(sketch, "E270", {"start": v(128.97, 2.8) * mm, "end": v(213.8, 2.8) * mm});
            skArc(sketch, "E271.0", {"start": v(212.68, -34.4) * mm, "mid": v(212.55, -34.81) * mm, "end": v(212.51, -35.23) * mm});
            skLineSegment(sketch, "E272.0", {"start": v(214.42, -30.35) * mm, "end": v(212.68, -34.4) * mm});
            skLineSegment(sketch, "E273", {"start": v(24.64, -46.5) * mm, "end": v(24.64, -31.34) * mm});
            skPoint(sketch, "E274.orphan", {"position": v(-3.14, -46.5) * mm});
            skLineSegment(sketch, "E275.trimOffspring", {"start": v(52.42, -75) * mm, "end": v(176.42, -75) * mm});
            skPoint(sketch, "E276.orphan", {"position": v(500, -75) * mm});
            skLineSegment(sketch, "E277.MirrorCS", {"start": v(167.42, -68.78) * mm, "end": v(161.42, -68.78) * mm});
            skSolve(sketch);
        }
        {
            var Q0;
            Q0=qCreatedBy(makeId("Front.planeOp"),FACE);
            var sketch = newSketch(context, id + "F11", { "sketchPlane" : qUnion([Q0])});
            skLineSegment(sketch, "E278.0", {"start": v(-170, -19) * mm, "end": v(-170, -75) * mm});
            skLineSegment(sketch, "E278.1", {"start": v(-140, -13) * mm, "end": v(-164, -13) * mm});
            skLineSegment(sketch, "E278.2", {"start": v(-110, -19) * mm, "end": v(-110, -75) * mm});
            skLineSegment(sketch, "E278.3", {"start": v(-170, -75) * mm, "end": v(-110, -75) * mm});
            skArc(sketch, "E278.4", {"start": v(-170, -19) * mm, "mid": v(-168.24, -14.76) * mm, "end": v(-164, -13) * mm});
            skArc(sketch, "E278.5", {"start": v(-110, -19) * mm, "mid": v(-111.76, -14.76) * mm, "end": v(-116, -13) * mm});
            skLineSegment(sketch, "E278.6", {"start": v(-140, -13) * mm, "end": v(-116, -13) * mm});
            skLineSegment(sketch, "E279.0", {"start": v(-30, -171) * mm, "end": v(-30, -225) * mm});
            skArc(sketch, "E279.1", {"start": v(-30, -171) * mm, "mid": v(-28.24, -166.76) * mm, "end": v(-24, -165) * mm});
            skLineSegment(sketch, "E279.2", {"start": v(0, -165) * mm, "end": v(-24, -165) * mm});
            skLineSegment(sketch, "E279.3", {"start": v(0, -165) * mm, "end": v(24, -165) * mm});
            skArc(sketch, "E279.4", {"start": v(30, -171) * mm, "mid": v(28.24, -166.76) * mm, "end": v(24, -165) * mm});
            skLineSegment(sketch, "E279.5", {"start": v(30, -171) * mm, "end": v(30, -225) * mm});
            skLineSegment(sketch, "E279.6", {"start": v(-30, -225) * mm, "end": v(30, -225) * mm});
            skLineSegment(sketch, "E280", {"start": v(-153, -44) * mm, "end": v(-127, -44) * mm, "construction": true});
            skLineSegment(sketch, "E281", {"start": v(-140, -21.5) * mm, "end": v(-140, -66.5) * mm, "construction": true});
            skCircle(sketch, "E282", {"center": v(-140, -21.5) * mm, "radius": 3 * mm});
            skCircle(sketch, "E283", {"center": v(-140, -66.5) * mm, "radius": 3 * mm});
            skLineSegment(sketch, "E284", {"start": v(-153, -13) * mm, "end": v(-153, -75) * mm, "construction": true});
            skLineSegment(sketch, "E285.MirrorCS", {"start": v(-127, -13) * mm, "end": v(-127, -75) * mm, "construction": true});
            skLineSegment(sketch, "E286.0", {"start": v(-481.28, -24) * mm, "end": v(-481.28, 21) * mm, "construction": true});
            skCircle(sketch, "E286.1", {"center": v(-481.28, -24) * mm, "radius": 3 * mm, "construction": true});
            skLineSegment(sketch, "E287", {"start": v(-13, -195) * mm, "end": v(13, -195) * mm, "construction": true});
            skLineSegment(sketch, "E288", {"start": v(0, -172.5) * mm, "end": v(0, -217.5) * mm, "construction": true});
            skCircle(sketch, "E289", {"center": v(0, -172.5) * mm, "radius": 3 * mm});
            skCircle(sketch, "E290", {"center": v(0, -217.5) * mm, "radius": 3 * mm});
            skLineSegment(sketch, "E291", {"start": v(-13, -165) * mm, "end": v(-13, -225) * mm, "construction": true});
            skLineSegment(sketch, "E292.MirrorCS", {"start": v(13, -165) * mm, "end": v(13, -225) * mm, "construction": true});
            skSolve(sketch);
        }
        {
            var Q0;
            Q0=qCreatedBy(makeId("Front.planeOp"),FACE);
            var sketch = newSketch(context, id + "F12", { "sketchPlane" : qUnion([Q0])});
            skLineSegment(sketch, "E293.0", {"start": v(-255, -126) * mm, "end": v(-255, -205) * mm});
            skLineSegment(sketch, "E293.1", {"start": v(-229, -225) * mm, "end": v(-223.5, -225) * mm});
            skLineSegment(sketch, "E293.2", {"start": v(-142.4, -192.17) * mm, "end": v(-229, -115.75) * mm});
            skLineSegment(sketch, "E293.3", {"start": v(-109.14, -192.17) * mm, "end": v(-142.4, -192.17) * mm});
            skLineSegment(sketch, "E293.4", {"start": v(-59.78, -197.17) * mm, "end": v(-104.21, -196.52) * mm});
            skLineSegment(sketch, "E293.5", {"start": v(-104.21, -196.52) * mm, "end": v(-109.14, -192.17) * mm});
            skLineSegment(sketch, "E293.6", {"start": v(-60.2, -225) * mm, "end": v(-59.78, -197.17) * mm});
            skLineSegment(sketch, "E293.7", {"start": v(-201.6, -139.93) * mm, "end": v(-203.34, -126) * mm});
            skLineSegment(sketch, "E294", {"start": v(-229, -205) * mm, "end": v(-8.61, -205) * mm, "construction": true});
            skLineSegment(sketch, "E295", {"start": v(-229, -205) * mm, "end": v(-229, -118.75) * mm, "construction": true});
            skLineSegment(sketch, "E296", {"start": v(-205, -205) * mm, "end": v(-205, -136.93) * mm, "construction": true});
            skLineSegment(sketch, "E297", {"start": v(-255, -126) * mm, "end": v(-203.34, -126) * mm});
            skLineSegment(sketch, "E298", {"start": v(-229, -205) * mm, "end": v(-229, -225) * mm});
            skLineSegment(sketch, "E299", {"start": v(-205, -205) * mm, "end": v(-205, -206.5) * mm});
            skPoint(sketch, "E300.orphan", {"position": v(-255, -225) * mm});
            skLineSegment(sketch, "E301", {"start": v(-255, -205) * mm, "end": v(-229, -205) * mm});
            skLineSegment(sketch, "E302", {"start": v(-203.5, -205) * mm, "end": v(-203.5, -225) * mm, "construction": true});
            skLineSegment(sketch, "E303", {"start": v(-205, -206.5) * mm, "end": v(-223.5, -225) * mm});
            skLineSegment(sketch, "E304.MirrorCS", {"start": v(-202, -206.5) * mm, "end": v(-183.5, -225) * mm});
            skLineSegment(sketch, "E305", {"start": v(-205, -205) * mm, "end": v(-202, -205) * mm});
            skLineSegment(sketch, "E306", {"start": v(-202, -205) * mm, "end": v(-202, -206.5) * mm});
            skLineSegment(sketch, "E307.trimOffspring", {"start": v(-183.5, -225) * mm, "end": v(-60.2, -225) * mm});
            skLineSegment(sketch, "E308.0", {"start": v(-500, 32.5) * mm, "end": v(-500, -46.5) * mm, "construction": true});
            skCircle(sketch, "E309.0", {"center": v(-481.28, -24) * mm, "radius": 3 * mm, "construction": true});
            skLineSegment(sketch, "E309.1", {"start": v(-481.28, -46.5) * mm, "end": v(-481.28, -24) * mm, "construction": true});
            skLineSegment(sketch, "E310.0", {"start": v(-481.28, -24) * mm, "end": v(-481.28, 21) * mm, "construction": true});
            skLineSegment(sketch, "E311.0", {"start": v(-481.28, -24) * mm, "end": v(-462, -24) * mm, "construction": true});
            skCircle(sketch, "E312.0", {"center": v(-242, -182.5) * mm, "radius": 3 * mm});
            skLineSegment(sketch, "E312.1", {"start": v(-242, -205) * mm, "end": v(-242, -182.5) * mm, "construction": true});
            skLineSegment(sketch, "E313.0", {"start": v(-242, -182.5) * mm, "end": v(-242, -137.5) * mm, "construction": true});
            skLineSegment(sketch, "E314.0", {"start": v(-242, -182.5) * mm, "end": v(-229, -182.5) * mm, "construction": true});
            skCircle(sketch, "E315", {"center": v(-242, -137.5) * mm, "radius": 3 * mm});
            skLineSegment(sketch, "E316.0.1", {"start": v(-255, -75) * mm, "end": v(-255, -225) * mm});
            skLineSegment(sketch, "E316.0.3", {"start": v(232.78, -205) * mm, "end": v(237.78, -182.5) * mm});
            skLineSegment(sketch, "E317.0", {"start": v(59.78, -197.17) * mm, "end": v(104.21, -196.52) * mm});
            skLineSegment(sketch, "E317.1", {"start": v(60.2, -225) * mm, "end": v(59.78, -197.17) * mm});
            skLineSegment(sketch, "E317.2", {"start": v(109.14, -192.17) * mm, "end": v(142.4, -192.17) * mm});
            skLineSegment(sketch, "E317.3", {"start": v(142.4, -192.17) * mm, "end": v(211.78, -130.95) * mm});
            skLineSegment(sketch, "E318.0", {"start": v(104.21, -196.52) * mm, "end": v(109.14, -192.17) * mm});
            skLineSegment(sketch, "E319", {"start": v(60.2, -225) * mm, "end": v(166.28, -225) * mm});
            skLineSegment(sketch, "E320", {"start": v(-8.61, -205) * mm, "end": v(-8.61, -225) * mm, "construction": true});
            skLineSegment(sketch, "E321.MirrorCS", {"start": v(184.78, -206.5) * mm, "end": v(166.28, -225) * mm});
            skLineSegment(sketch, "E322.MirrorCS", {"start": v(187.78, -206.5) * mm, "end": v(206.28, -225) * mm});
            skLineSegment(sketch, "E323.MirrorCS", {"start": v(211.78, -225) * mm, "end": v(206.28, -225) * mm});
            skLineSegment(sketch, "E324.MirrorCS", {"start": v(211.78, -205) * mm, "end": v(211.78, -225) * mm});
            skLineSegment(sketch, "E325.MirrorCS", {"start": v(237.78, -205) * mm, "end": v(211.78, -205) * mm});
            skCircle(sketch, "E326.MirrorC", {"center": v(224.78, -182.5) * mm, "radius": 3 * mm});
            skLineSegment(sketch, "E327.MirrorCS", {"start": v(187.78, -205) * mm, "end": v(187.78, -206.5) * mm});
            skLineSegment(sketch, "E328.MirrorCS", {"start": v(184.78, -205) * mm, "end": v(184.78, -206.5) * mm});
            skLineSegment(sketch, "E329.MirrorCS", {"start": v(187.78, -205) * mm, "end": v(184.78, -205) * mm});
            skLineSegment(sketch, "E330", {"start": v(237.78, -108) * mm, "end": v(237.78, -182.5) * mm});
            skLineSegment(sketch, "E331.trimOffspring", {"start": v(206.28, -225) * mm, "end": v(211.78, -225) * mm});
            skLineSegment(sketch, "E332.bottom", {"start": v(-229, -118.75) * mm, "end": v(-232, -118.75) * mm});
            skLineSegment(sketch, "E332.left", {"start": v(-229, -118.75) * mm, "end": v(-229, -115.75) * mm});
            skLineSegment(sketch, "E332.right", {"start": v(-232, -118.75) * mm, "end": v(-232, -113.1) * mm});
            skLineSegment(sketch, "E333.trimOffspring", {"start": v(-201.6, -139.93) * mm, "end": v(-232, -113.1) * mm});
            skLineSegment(sketch, "E334.top", {"start": v(211.78, -160.83) * mm, "end": v(214.78, -160.83) * mm});
            skLineSegment(sketch, "E334.left", {"start": v(211.78, -130.95) * mm, "end": v(211.78, -160.83) * mm});
            skLineSegment(sketch, "E334.right", {"start": v(214.78, -128.3) * mm, "end": v(214.78, -160.83) * mm});
            skLineSegment(sketch, "E335.trimOffspring", {"start": v(214.78, -128.3) * mm, "end": v(237.78, -108) * mm});
            skSolve(sketch);
        }
        {
            var Q0;
            Q0=qCreatedBy(makeId("Front.planeOp"),FACE);
            var sketch = newSketch(context, id + "F13", { "sketchPlane" : qUnion([Q0])});
            skLineSegment(sketch, "E336.0", {"start": v(0, -165) * mm, "end": v(0, -82.5) * mm});
            skArc(sketch, "E336.1", {"start": v(0, -82.5) * mm, "mid": v(103.74, -81.42) * mm, "end": v(207.44, -78.17) * mm});
            skLineSegment(sketch, "E336.2", {"start": v(0, -165) * mm, "end": v(24, -165) * mm});
            skLineSegment(sketch, "E336.3", {"start": v(30, -171) * mm, "end": v(30, -212.17) * mm});
            skArc(sketch, "E336.4", {"start": v(30, -171) * mm, "mid": v(28.24, -166.76) * mm, "end": v(24, -165) * mm});
            skLineSegment(sketch, "E336.5", {"start": v(89.5, -212.17) * mm, "end": v(30, -212.17) * mm});
            skLineSegment(sketch, "E336.7", {"start": v(209.53, -80.4) * mm, "end": v(210.53, -104.39) * mm});
            skArc(sketch, "E336.8", {"start": v(209.53, -80.4) * mm, "mid": v(208.89, -79.02) * mm, "end": v(207.45, -78.5) * mm});
            skLineSegment(sketch, "E336.9", {"start": v(207.45, -78.5) * mm, "end": v(208.56, -107.1) * mm, "construction": true});
            skLineSegment(sketch, "E337.0", {"start": v(89.5, -212.17) * mm, "end": v(209.86, -105.97) * mm});
            skArc(sketch, "E338.0", {"start": v(210.53, -104.39) * mm, "mid": v(210.37, -105.25) * mm, "end": v(209.86, -105.97) * mm});
            skLineSegment(sketch, "E339", {"start": v(207.44, -78.17) * mm, "end": v(207.45, -78.5) * mm});
            skSolve(sketch);
        }
        {
            var Q0;
            Q0 = qSketchRegion(id + "F6", true);
            var Q1;
            Q1 = qSketchRegion(id + "F8", true);
            var Q2;
            Q2 = qSketchRegion(id + "F7", true);
            extrude(context, id + "F14", {"entities" : qUnion([Q0, Q1, Q2]), "endBound" : BoundingType.SYMMETRIC, "depth" : (getVariable(context, 'eTole')) * mm});
        }
        {
            var Q0;
            Q0 = qSketchRegion(id + "F13", true);
            extrude(context, id + "F15", {"entities" : qUnion([Q0]), "depth" : (2 * getVariable(context, 'eTole') + getVariable(context, 'eProfil')) * mm, "offsetDistance" : 25 * mm, "hasSecondDirection" : true, "secondDirectionOppositeDirection" : false, "secondDirectionDepth" : (2 * getVariable(context, 'eTole')) * mm});
        }
        {
            var Q0;
            Q0=makeQuery(id+"F14.opExtrude","SWEPT_BODY",BODY,{"disambiguationData":[OSD([sQuery(id+"F6.wireOp",EDGE,"E39.1"),sQuery(id+"F6.wireOp",EDGE,"E39.2"),sQuery(id+"F6.wireOp",EDGE,"E39.3"),sQuery(id+"F6.wireOp",EDGE,"E40"),sQuery(id+"F6.wireOp",EDGE,"E41.trimOffspring"),sQuery(id+"F6.wireOp",EDGE,"E47"),sQuery(id+"F6.wireOp",EDGE,"E49"),sQuery(id+"F6.wireOp",EDGE,"E50"),sQuery(id+"F6.wireOp",EDGE,"E52"),sQuery(id+"F6.wireOp",EDGE,"E54"),sQuery(id+"F6.wireOp",EDGE,"E55"),sQuery(id+"F6.wireOp",EDGE,"E56"),sQuery(id+"F6.wireOp",EDGE,"E57"),sQuery(id+"F6.wireOp",EDGE,"E58"),sQuery(id+"F6.wireOp",EDGE,"E59"),sQuery(id+"F6.wireOp",EDGE,"E60"),sQuery(id+"F6.wireOp",EDGE,"E61"),sQuery(id+"F6.wireOp",EDGE,"E62"),sQuery(id+"F6.wireOp",EDGE,"E63"),sQuery(id+"F6.wireOp",EDGE,"E64"),sQuery(id+"F6.wireOp",EDGE,"E65"),sQuery(id+"F6.wireOp",EDGE,"E67"),sQuery(id+"F6.wireOp",EDGE,"E68"),sQuery(id+"F6.wireOp",EDGE,"E69"),sQuery(id+"F6.wireOp",EDGE,"E70"),sQuery(id+"F6.wireOp",EDGE,"E71"),sQuery(id+"F6.wireOp",EDGE,"E72"),sQuery(id+"F6.wireOp",EDGE,"E73"),sQuery(id+"F6.wireOp",EDGE,"E74"),sQuery(id+"F6.wireOp",EDGE,"E75"),sQuery(id+"F6.wireOp",EDGE,"E76"),sQuery(id+"F6.wireOp",EDGE,"E77.filletArc"),sQuery(id+"F6.wireOp",EDGE,"E78.trimOffspring"),sQuery(id+"F6.wireOp",EDGE,"E79.filletArc"),sQuery(id+"F6.wireOp",EDGE,"E80.filletArc"),sQuery(id+"F6.wireOp",EDGE,"E81.filletArc"),sQuery(id+"F6.wireOp",EDGE,"E82.filletArc"),sQuery(id+"F6.wireOp",EDGE,"E83.0"),sQuery(id+"F6.wireOp",EDGE,"E84"),sQuery(id+"F6.wireOp",EDGE,"E85")])]});
            var Q1;
            Q1=qCreatedBy(id+"F3.planeOp",FACE);
            mirror(context, id + "F16", {"operationType" : NewBodyOperationType.ADD, "entities" : qUnion([Q0]), "mirrorPlane" : qUnion([Q1])});
        }
        {
            var Q0;
            Q0=makeQuery(id+"F14.opExtrude","SWEPT_BODY",BODY,{"disambiguationData":[OSD([sQuery(id+"F7.wireOp",EDGE,"E86.0"),sQuery(id+"F7.wireOp",EDGE,"E87.0"),sQuery(id+"F7.wireOp",EDGE,"E87.1"),sQuery(id+"F7.wireOp",EDGE,"E87.2"),sQuery(id+"F7.wireOp",EDGE,"E88"),sQuery(id+"F7.wireOp",EDGE,"E89.trimOffspring"),sQuery(id+"F7.wireOp",EDGE,"E91"),sQuery(id+"F7.wireOp",EDGE,"E95"),sQuery(id+"F7.wireOp",EDGE,"E96"),sQuery(id+"F7.wireOp",EDGE,"E97"),sQuery(id+"F7.wireOp",EDGE,"E98"),sQuery(id+"F7.wireOp",EDGE,"E99"),sQuery(id+"F7.wireOp",EDGE,"E102"),sQuery(id+"F7.wireOp",EDGE,"E103"),sQuery(id+"F7.wireOp",EDGE,"E104"),sQuery(id+"F7.wireOp",EDGE,"E105"),sQuery(id+"F7.wireOp",EDGE,"E106"),sQuery(id+"F7.wireOp",EDGE,"E107"),sQuery(id+"F7.wireOp",EDGE,"E108"),sQuery(id+"F7.wireOp",EDGE,"E109"),sQuery(id+"F7.wireOp",EDGE,"E110"),sQuery(id+"F7.wireOp",EDGE,"E111"),sQuery(id+"F7.wireOp",EDGE,"E112"),sQuery(id+"F7.wireOp",EDGE,"E113"),sQuery(id+"F7.wireOp",EDGE,"E114")])]});
            var Q1;
            Q1=makeQuery(id+"F15.opExtrude","SWEPT_BODY",BODY,{"disambiguationData":[OSD([sQuery(id+"F13.wireOp",EDGE,"E336.0"),sQuery(id+"F13.wireOp",EDGE,"E336.1"),sQuery(id+"F13.wireOp",EDGE,"E336.2"),sQuery(id+"F13.wireOp",EDGE,"E336.3"),sQuery(id+"F13.wireOp",EDGE,"E336.4"),sQuery(id+"F13.wireOp",EDGE,"E336.5"),sQuery(id+"F13.wireOp",EDGE,"E336.7"),sQuery(id+"F13.wireOp",EDGE,"E336.8"),sQuery(id+"F13.wireOp",EDGE,"E337.0"),sQuery(id+"F13.wireOp",EDGE,"E338.0"),sQuery(id+"F13.wireOp",EDGE,"E339")])]});
            var Q2;
            Q2=qCreatedBy(makeId("Right.planeOp"),FACE);
            mirror(context, id + "F17", {"operationType" : NewBodyOperationType.ADD, "entities" : qUnion([Q0, Q1]), "mirrorPlane" : qUnion([Q2])});
        }
        {
            var Q0;
            Q0=makeQuery(id+"F14.opExtrude","SWEPT_BODY",BODY,{"disambiguationData":[OSD([sQuery(id+"F8.wireOp",EDGE,"E130.0"),sQuery(id+"F8.wireOp",EDGE,"E130.1"),sQuery(id+"F8.wireOp",EDGE,"E130.3"),sQuery(id+"F8.wireOp",EDGE,"E131"),sQuery(id+"F8.wireOp",EDGE,"E132.trimOffspring"),sQuery(id+"F8.wireOp",EDGE,"E133"),sQuery(id+"F8.wireOp",EDGE,"E136"),sQuery(id+"F8.wireOp",EDGE,"E138"),sQuery(id+"F8.wireOp",EDGE,"E139"),sQuery(id+"F8.wireOp",EDGE,"E141"),sQuery(id+"F8.wireOp",EDGE,"E142"),sQuery(id+"F8.wireOp",EDGE,"E144"),sQuery(id+"F8.wireOp",EDGE,"E146"),sQuery(id+"F8.wireOp",EDGE,"E147"),sQuery(id+"F8.wireOp",EDGE,"E148"),sQuery(id+"F8.wireOp",EDGE,"E149"),sQuery(id+"F8.wireOp",EDGE,"E150"),sQuery(id+"F8.wireOp",EDGE,"E151"),sQuery(id+"F8.wireOp",EDGE,"E152"),sQuery(id+"F8.wireOp",EDGE,"E153.trimOffspring"),sQuery(id+"F8.wireOp",EDGE,"E154"),sQuery(id+"F8.wireOp",EDGE,"E155"),sQuery(id+"F8.wireOp",EDGE,"E156"),sQuery(id+"F8.wireOp",EDGE,"E157"),sQuery(id+"F8.wireOp",EDGE,"E158"),sQuery(id+"F8.wireOp",EDGE,"E159"),sQuery(id+"F8.wireOp",EDGE,"E160"),sQuery(id+"F8.wireOp",EDGE,"E161"),sQuery(id+"F8.wireOp",EDGE,"E162"),sQuery(id+"F8.wireOp",EDGE,"E163"),sQuery(id+"F8.wireOp",EDGE,"E164"),sQuery(id+"F8.wireOp",EDGE,"E165.filletArc"),sQuery(id+"F8.wireOp",EDGE,"E166.0")])]});
            var Q1;
            Q1=qCreatedBy(id+"F4.planeOp",FACE);
            mirror(context, id + "F18", {"operationType" : NewBodyOperationType.ADD, "entities" : qUnion([Q0]), "mirrorPlane" : qUnion([Q1])});
        }
    });
